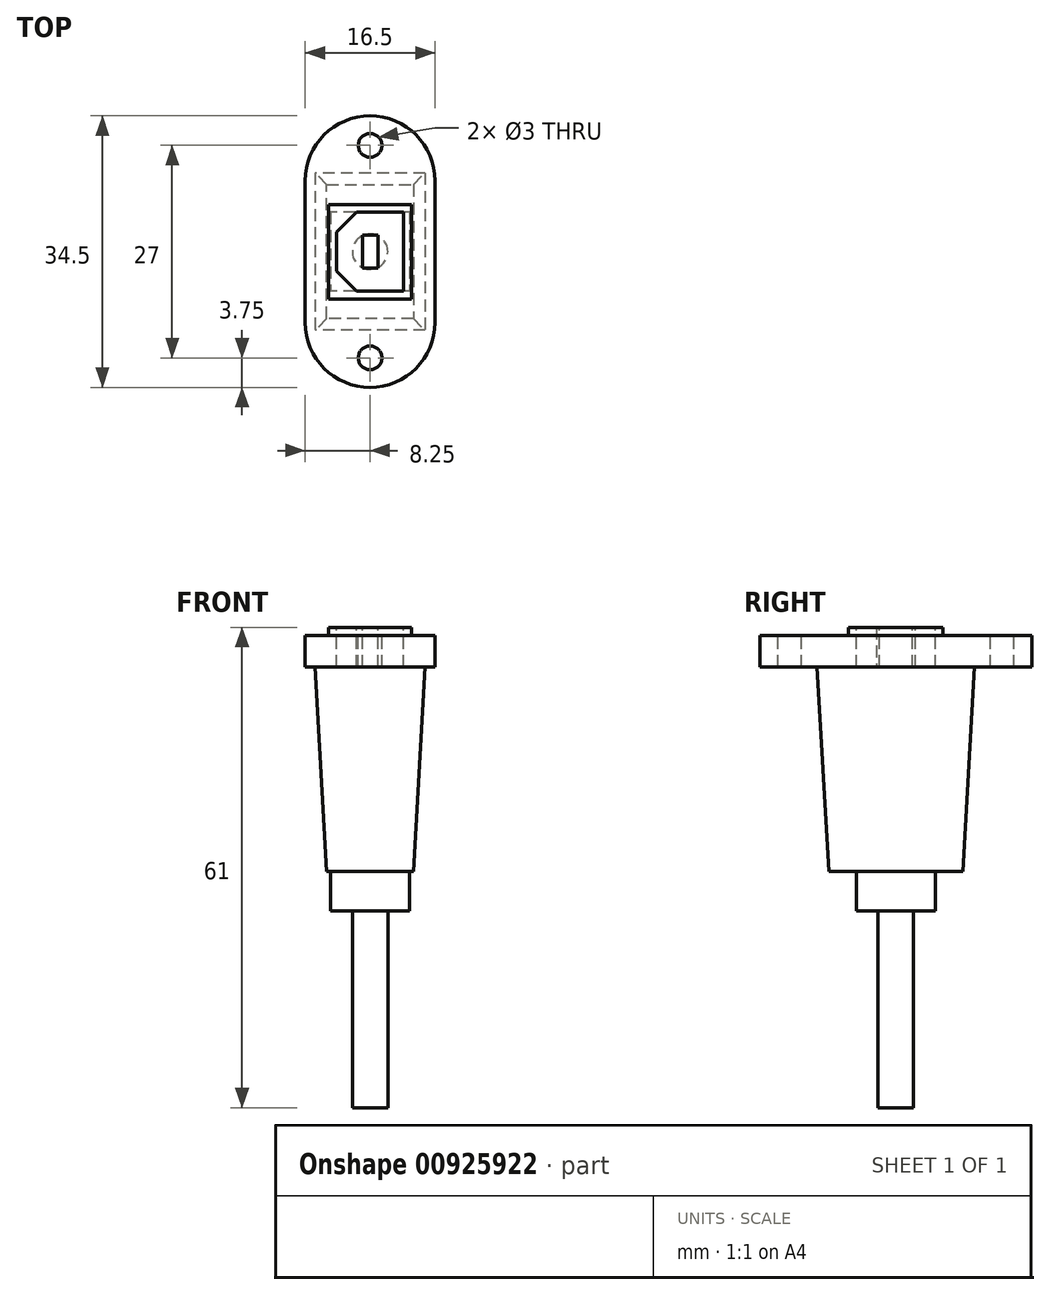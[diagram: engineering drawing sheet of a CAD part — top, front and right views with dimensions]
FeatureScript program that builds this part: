
annotation { "Feature Type Name" : "Feature", "Feature Type Description" : "" }
export const myFeature = defineFeature(function(context is Context, id is Id, definition is map)
    precondition{}
    {
        {
            var Q0;
            Q0=qCreatedBy(makeId("Top.planeOp"),FACE);
            var sketch = newSketch(context, id + "F0", { "sketchPlane" : qUnion([Q0])});
            skPoint(sketch, "E0.middle", {"position": v(0, 0) * mm});
            skLineSegment(sketch, "E1.bottom", {"start": v(8.25, -9) * mm, "end": v(-8.25, -9) * mm});
            skLineSegment(sketch, "E1.top", {"start": v(8.25, 9) * mm, "end": v(-8.25, 9) * mm});
            skArc(sketch, "E2", {"start": v(8.25, 9) * mm, "mid": v(0, 17.25) * mm, "end": v(-8.25, 9) * mm});
            skArc(sketch, "E3", {"start": v(8.25, -9) * mm, "mid": v(0, -17.25) * mm, "end": v(-8.25, -9) * mm});
            skCircle(sketch, "E4", {"center": v(0, 13.5) * mm, "radius": 1.5 * mm});
            skCircle(sketch, "E5", {"center": v(0, -13.5) * mm, "radius": 1.5 * mm});
            skSolve(sketch);
        }
        {
            var Q0;
            Q0=makeQuery(id+"F0.imprint","IMPRINT",FACE,{"disambiguationData":[TD([[makeQuery(id+"F0.imprint","IMPRINT",EDGE,{"derivedFrom":sQuery(id+"F0.wireOp",EDGE,"E0.bottom")}),1.0]])]});
            var Q1;
            Q1=makeQuery(id+"F0.imprint","IMPRINT",FACE,{"disambiguationData":[TD([[makeQuery(id+"F0.imprint","IMPRINT",EDGE,{"derivedFrom":sQuery(id+"F0.wireOp",EDGE,"E1.top")}),-1.0]])]});
            var Q2;
            Q2=makeQuery(id+"F0.imprint","IMPRINT",FACE,{"disambiguationData":[TD([[makeQuery(id+"F0.imprint","IMPRINT",EDGE,{"derivedFrom":sQuery(id+"F0.wireOp",EDGE,"E1.bottom")}),1.0]])]});
            extrude(context, id + "F1", {"entities" : qUnion([Q0, Q1, Q2]), "oppositeDirection" : true, "depth" : 4 * mm, "offsetDistance" : 25 * mm});
        }
        {
            var Q0;
            Q0=makeQuery(id+"F1.opExtrude","CAP_FACE",FACE,{"disambiguationData":[OSD([sQuery(id+"F0.wireOp",EDGE,"E0.bottom"),sQuery(id+"F0.wireOp",EDGE,"E0.top"),sQuery(id+"F0.wireOp",EDGE,"E0.left"),sQuery(id+"F0.wireOp",EDGE,"E0.right"),sQuery(id+"F0.wireOp",EDGE,"E1.left"),sQuery(id+"F0.wireOp",EDGE,"E1.right"),sQuery(id+"F0.wireOp",EDGE,"E2"),sQuery(id+"F0.wireOp",EDGE,"E3"),sQuery(id+"F0.wireOp",EDGE,"E4"),sQuery(id+"F0.wireOp",EDGE,"E5")])],"isStart":false});
            var sketch = newSketch(context, id + "F2", { "sketchPlane" : qUnion([Q0])});
            skLineSegment(sketch, "E6.bottom", {"start": v(7, -10) * mm, "end": v(-7, -10) * mm});
            skLineSegment(sketch, "E6.top", {"start": v(7, 10) * mm, "end": v(-7, 10) * mm});
            skLineSegment(sketch, "E6.left", {"start": v(7, -10) * mm, "end": v(7, 10) * mm});
            skLineSegment(sketch, "E6.right", {"start": v(-7, -10) * mm, "end": v(-7, 10) * mm});
            skPoint(sketch, "E6.middle", {"position": v(0, 0) * mm});
            skSolve(sketch);
        }
        {
            var Q0;
            Q0=qSketchRegion(id+"F2",true);
            extrude(context, id + "F3", {"entities" : qUnion([Q0]), "operationType" : NewBodyOperationType.ADD, "depth" : 26 * mm, "offsetDistance" : 25 * mm});
        }
        {
            var Q0;
            Q0=makeQuery(id+"F3.opExtrude","CAP_EDGE",EDGE,{"disambiguationData":[OSD([sQuery(id+"F2.wireOp",EDGE,"E6.top")])],"isStart":false});
            var Q1;
            Q1=makeQuery(id+"F3.opExtrude","CAP_EDGE",EDGE,{"disambiguationData":[OSD([sQuery(id+"F2.wireOp",EDGE,"E6.bottom")])],"isStart":false});
            var Q2;
            Q2=makeQuery(id+"F3.opExtrude","CAP_EDGE",EDGE,{"disambiguationData":[OSD([sQuery(id+"F2.wireOp",EDGE,"E6.left")])],"isStart":false});
            var Q3;
            Q3=makeQuery(id+"F3.opExtrude","CAP_EDGE",EDGE,{"disambiguationData":[OSD([sQuery(id+"F2.wireOp",EDGE,"E6.right")])],"isStart":false});
            chamfer(context, id + "F4", {"entities" : qUnion([Q0, Q1, Q2, Q3]), "chamferType" : ChamferType.TWO_OFFSETS, "width1" : 1.5 * mm, "oppositeDirection" : false, "width2" : 26 * mm, "tangentPropagation" : true});
        }
        {
            var Q0;
            Q0=makeQuery(id+"F3.opExtrude","CAP_FACE",FACE,{"disambiguationData":[OSD([sQuery(id+"F2.wireOp",EDGE,"E6.bottom"),sQuery(id+"F2.wireOp",EDGE,"E6.top"),sQuery(id+"F2.wireOp",EDGE,"E6.left"),sQuery(id+"F2.wireOp",EDGE,"E6.right")])],"isStart":false});
            var sketch = newSketch(context, id + "F5", { "sketchPlane" : qUnion([Q0])});
            skLineSegment(sketch, "E7.bottom", {"start": v(5, -5) * mm, "end": v(-5, -5) * mm});
            skLineSegment(sketch, "E7.top", {"start": v(5, 5) * mm, "end": v(-5, 5) * mm});
            skLineSegment(sketch, "E7.left", {"start": v(5, -5) * mm, "end": v(5, 5) * mm});
            skLineSegment(sketch, "E7.right", {"start": v(-5, -5) * mm, "end": v(-5, 5) * mm});
            skPoint(sketch, "E7.middle", {"position": v(0, 0) * mm});
            skSolve(sketch);
        }
        {
            var Q0;
            Q0=qSketchRegion(id+"F5",true);
            extrude(context, id + "F6", {"entities" : qUnion([Q0]), "operationType" : NewBodyOperationType.ADD, "depth" : 5 * mm, "offsetDistance" : 25 * mm});
        }
        {
            var Q0;
            Q0=makeQuery(id+"F6.opExtrude","CAP_FACE",FACE,{"disambiguationData":[OSD([sQuery(id+"F5.wireOp",EDGE,"E7.bottom"),sQuery(id+"F5.wireOp",EDGE,"E7.top"),sQuery(id+"F5.wireOp",EDGE,"E7.left"),sQuery(id+"F5.wireOp",EDGE,"E7.right")])],"isStart":false});
            var sketch = newSketch(context, id + "F7", { "sketchPlane" : qUnion([Q0])});
            skCircle(sketch, "E8", {"center": v(0, 0) * mm, "radius": 2.25 * mm});
            skSolve(sketch);
        }
        {
            var Q0;
            Q0=qSketchRegion(id+"F7",true);
            extrude(context, id + "F8", {"entities" : qUnion([Q0]), "operationType" : NewBodyOperationType.ADD, "depth" : 25 * mm, "offsetDistance" : 25 * mm});
        }
        {
            var Q0;
            Q0=makeQuery(id+"F1.opExtrude","SWEPT_FACE",FACE,{"disambiguationData":[OSD([sQuery(id+"F0.wireOp",EDGE,"E1.bottom")])]});
            extrude(context, id + "F9", {"entities" : qUnion([Q0]), "operationType" : NewBodyOperationType.ADD, "depth" : 18 * mm, "offsetDistance" : 25 * mm});
        }
        {
            var Q0;
            {var subQ0=sQuery(id+"F0.wireOp",EDGE,"E1.bottom");Q0=makeQuery(id+"F9.boolean.opBoolean","MERGE",FACE,{"derivedFrom":[makeQuery(id+"F1.opExtrude","CAP_FACE",FACE,{"disambiguationData":[OSD([subQ0,sQuery(id+"F0.wireOp",EDGE,"E3"),sQuery(id+"F0.wireOp",EDGE,"E5")])],"isStart":true}),makeQuery(id+"F1.opExtrude","CAP_FACE",FACE,{"disambiguationData":[OSD([sQuery(id+"F0.wireOp",EDGE,"E1.top"),sQuery(id+"F0.wireOp",EDGE,"E2"),sQuery(id+"F0.wireOp",EDGE,"E4")])],"isStart":true}),makeQuery(id+"F9.opExtrude","SWEPT_FACE",FACE,{"disambiguationData":[OSD([subQ0]),TDD([makeQuery(id+"F1.opExtrude","CAP_EDGE",EDGE,{"disambiguationData":[OSD([subQ0])],"isStart":true})])]})]});}
            var sketch = newSketch(context, id + "F10", { "sketchPlane" : qUnion([Q0])});
            skLineSegment(sketch, "E9.bottom", {"start": v(5.25, 6) * mm, "end": v(-5.25, 6) * mm});
            skLineSegment(sketch, "E9.top", {"start": v(5.25, -6) * mm, "end": v(-5.25, -6) * mm});
            skLineSegment(sketch, "E9.left", {"start": v(5.25, 6) * mm, "end": v(5.25, -6) * mm});
            skLineSegment(sketch, "E9.right", {"start": v(-5.25, 6) * mm, "end": v(-5.25, -6) * mm});
            skPoint(sketch, "E9.middle", {"position": v(0, 0) * mm});
            skSolve(sketch);
        }
        {
            var Q0;
            Q0 = qSketchRegion(id + "F10", true);
            extrude(context, id + "F11", {"entities" : qUnion([Q0]), "operationType" : NewBodyOperationType.ADD, "depth" : 1 * mm, "offsetDistance" : 25 * mm});
        }
        {
            var Q0;
            Q0=makeQuery(id+"F11.opExtrude","CAP_FACE",FACE,{"disambiguationData":[OSD([sQuery(id+"F10.wireOp",EDGE,"E9.bottom"),sQuery(id+"F10.wireOp",EDGE,"E9.top"),sQuery(id+"F10.wireOp",EDGE,"E9.left"),sQuery(id+"F10.wireOp",EDGE,"E9.right")])],"isStart":false});
            var sketch = newSketch(context, id + "F12", { "sketchPlane" : qUnion([Q0])});
            skSolve(sketch);
        }
        {
            var Q0;
            Q0=makeQuery(id+"F12.imprint","IMPRINT",FACE,{"disambiguationData":[TD([[makeQuery(id+"F12.imprint","IMPRINT",EDGE,{"derivedFrom":makeQuery(id+"F11.opExtrude","CAP_EDGE",EDGE,{"disambiguationData":[OSD([sQuery(id+"F10.wireOp",EDGE,"E9.bottom")])],"isStart":false})}),1.0]])]});
            var sketch = newSketch(context, id + "F13", { "sketchPlane" : qUnion([Q0])});
            skLineSegment(sketch, "E10.bottom", {"start": v(4.25, -5) * mm, "end": v(-4.25, -5) * mm});
            skLineSegment(sketch, "E10.top", {"start": v(4.25, 5) * mm, "end": v(-4.25, 5) * mm});
            skLineSegment(sketch, "E10.left", {"start": v(4.25, -5) * mm, "end": v(4.25, 5) * mm});
            skLineSegment(sketch, "E10.right", {"start": v(-4.25, -5) * mm, "end": v(-4.25, 5) * mm});
            skPoint(sketch, "E10.middle", {"position": v(0, 0) * mm});
            skLineSegment(sketch, "E11.bottom", {"start": v(0.99, -2.11) * mm, "end": v(-0.99, -2.11) * mm});
            skLineSegment(sketch, "E11.top", {"start": v(0.99, 2.11) * mm, "end": v(-0.99, 2.11) * mm});
            skLineSegment(sketch, "E11.left", {"start": v(0.99, -2.11) * mm, "end": v(0.99, 2.11) * mm});
            skLineSegment(sketch, "E11.right", {"start": v(-0.99, -2.11) * mm, "end": v(-0.99, 2.11) * mm});
            skSolve(sketch);
        }
        {
            var Q0;
            Q0 = qSketchRegion(id + "F13", true);
            extrude(context, id + "F14", {"entities" : qUnion([Q0]), "operationType" : NewBodyOperationType.REMOVE, "oppositeDirection" : true, "depth" : 5 * mm, "offsetDistance" : 25 * mm});
        }
        {
            var Q0;
            Q0=makeQuery(id+"F14.boolean.opBoolean","COPY",EDGE,{"derivedFrom":makeQuery(id+"F14.opExtrude","SWEPT_EDGE",EDGE,{"disambiguationData":[OSD([sQuery(id+"F13.wireOp",EDGE,"E10.bottom"),sQuery(id+"F13.wireOp",EDGE,"E10.right")])]})});
            var Q1;
            Q1=makeQuery(id+"F14.boolean.opBoolean","COPY",EDGE,{"derivedFrom":makeQuery(id+"F14.opExtrude","SWEPT_EDGE",EDGE,{"disambiguationData":[OSD([sQuery(id+"F13.wireOp",EDGE,"E10.top"),sQuery(id+"F13.wireOp",EDGE,"E10.right")])]})});
            chamfer(context, id + "F15", {"entities" : qUnion([Q0, Q1]), "width" : 2.5 * mm, "tangentPropagation" : true});
        }
    });
